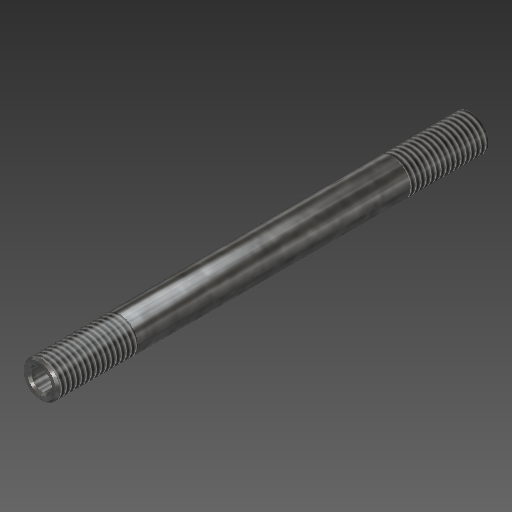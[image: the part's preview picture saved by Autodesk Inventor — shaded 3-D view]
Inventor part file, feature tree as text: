
AUTODESK INVENTOR PART (.ipt)
format: ipt  version: 2018 (Build 220112000, 112)  size: 142,336 bytes
history: native  units: mm
features: thread x2, extrude x1, plane x1, chamfer x1, sketch x1
ambient origin geometry x8: Origin, YZ Plane, XZ Plane, XY Plane, X Axis, Y Axis, Z Axis, Center Point
bodies: Solid1 (feature_tree)
feature tree (6):
  extrude  "Extrusion1"  Depth=108.2mm
  thread  "Thread1"  [1 undecoded]
  plane  "Work Plane1"
  thread  "Thread2"  [1 undecoded]
  chamfer  "Chamfer2"  Distance=20.0mm
  sketch  "Sketch1"  dims[d0=9.0mm d1=5.12mm d2=108.2mm d3=0.0mm d4=20.0mm d5=0.0mm d9=20.0mm d10=0.0mm d11=0.5mm d12=2.0mm d13=45.0deg]
note: 2 required parameter values undecoded (feature->parameter linkage not recoverable at this tier; creation-order binding heuristic only, values carry confidence <= 0.55)
